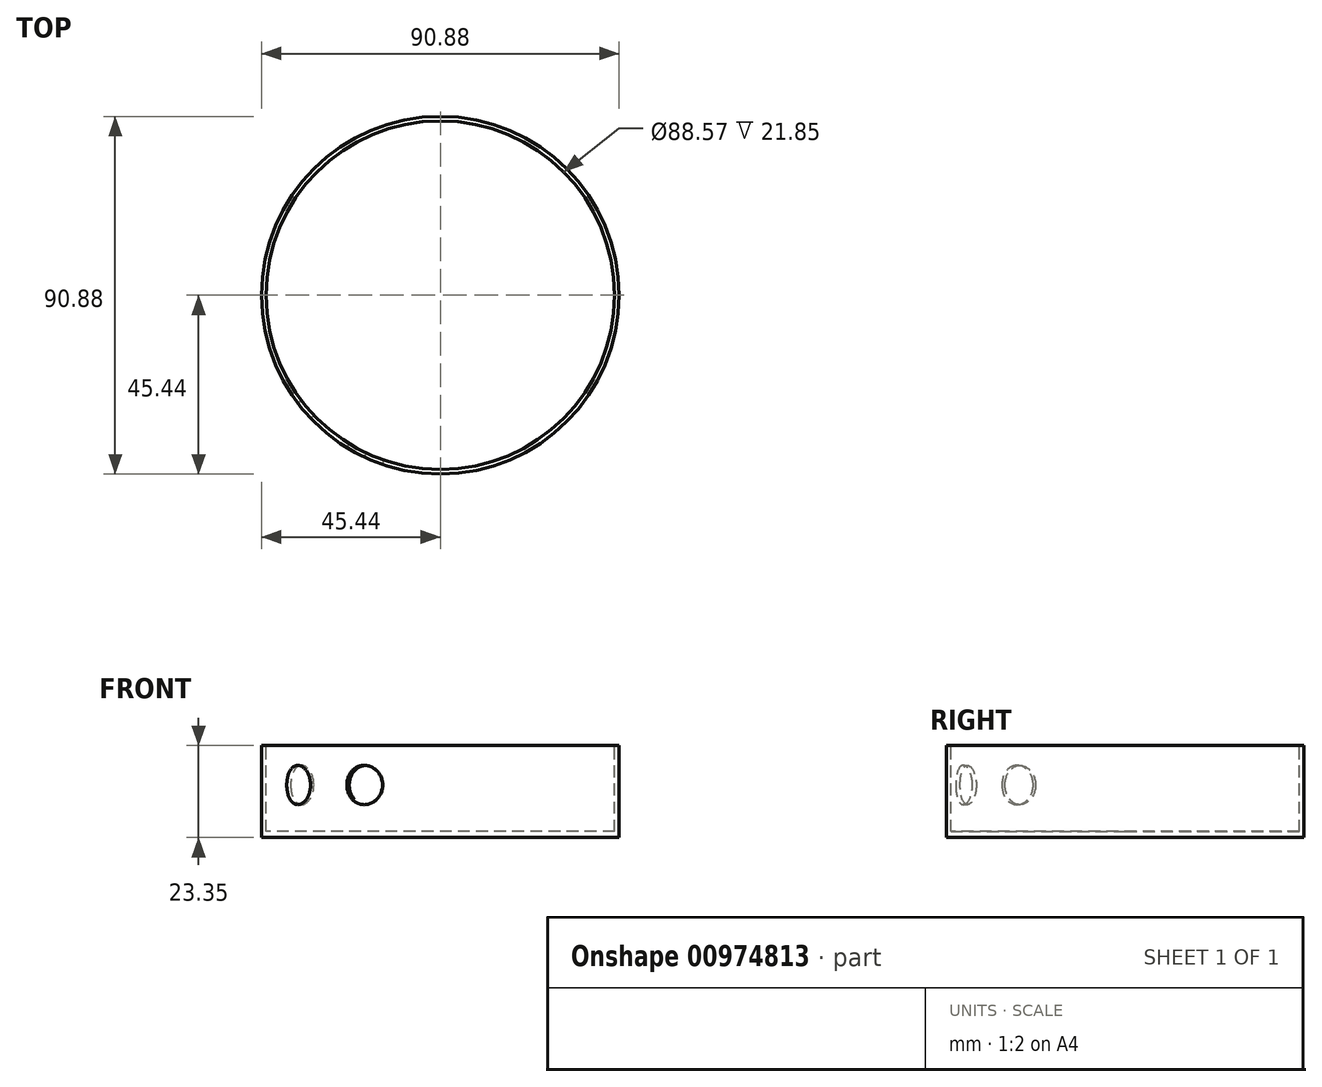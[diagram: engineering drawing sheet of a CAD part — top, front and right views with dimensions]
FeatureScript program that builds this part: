
annotation { "Feature Type Name" : "Feature", "Feature Type Description" : "" }
export const myFeature = defineFeature(function(context is Context, id is Id, definition is map)
    precondition{}
    {
        {
            var Q0;
            Q0=qCreatedBy(makeId("Top.planeOp"),FACE);
            var sketch = newSketch(context, id + "F0", { "sketchPlane" : qUnion([Q0])});
            skCircle(sketch, "E0", {"center": v(0, 0) * mm, "radius": 45.44 * mm});
            skSolve(sketch);
        }
        {
            var Q0;
            Q0 = qSketchRegion(id + "F0", true);
            extrude(context, id + "F1", {"entities" : qUnion([Q0]), "depth" : 23.35 * mm, "offsetDistance" : 25 * mm});
        }
        {
            var Q0;
            Q0=makeQuery(id+"F1.opExtrude","CAP_FACE",FACE,{"disambiguationData":[OSD([sQuery(id+"F0.wireOp",EDGE,"E0")])],"isStart":false});
            var sketch = newSketch(context, id + "F2", { "sketchPlane" : qUnion([Q0])});
            skCircle(sketch, "E1", {"center": v(0, 0) * mm, "radius": 44.29 * mm});
            skSolve(sketch);
        }
        {
            var Q0;
            Q0 = qSketchRegion(id + "F2", true);
            extrude(context, id + "F3", {"entities" : qUnion([Q0]), "operationType" : NewBodyOperationType.REMOVE, "oppositeDirection" : true, "depth" : 23.35 * mm - 1.5 * mm, "offsetDistance" : 25 * mm});
        }
        {
            var Q0;
            Q0=makeQuery(id+"F1.opExtrude","CAP_FACE",FACE,{"disambiguationData":[OSD([sQuery(id+"F0.wireOp",EDGE,"E0")])],"isStart":false});
            var sketch = newSketch(context, id + "F4", { "sketchPlane" : qUnion([Q0])});
            skSolve(sketch);
        }
        {
            var Q0;
            Q0=makeQuery(id+"F4.imprint","IMPRINT",FACE,{"disambiguationData":[TD([[makeQuery(id+"F4.imprint","IMPRINT",EDGE,{"derivedFrom":makeQuery(id+"F1.opExtrude","CAP_EDGE",EDGE,{"disambiguationData":[OSD([sQuery(id+"F0.wireOp",EDGE,"E0")])],"isStart":false})}),1.0]])]});
            var sketch = newSketch(context, id + "F5", { "sketchPlane" : qUnion([Q0])});
            skLineSegment(sketch, "E2", {"start": v(0, 0) * mm, "end": v(-23.74, -38.74) * mm});
            skLineSegment(sketch, "E3", {"start": v(0, 0) * mm, "end": v(-14.69, -43) * mm});
            skArc(sketch, "E4", {"start": v(-23.74, -38.74) * mm, "mid": v(-19.33, -41.12) * mm, "end": v(-14.69, -43) * mm});
            skLineSegment(sketch, "E5.2.0", {"start": v(0, 0) * mm, "end": v(-32.95, -31.28) * mm});
            skLineSegment(sketch, "E5.2.1", {"start": v(0, 0) * mm, "end": v(-39, -23.31) * mm});
            skArc(sketch, "E6", {"start": v(-39, -23.31) * mm, "mid": v(-42.8, -32.48) * mm, "end": v(-32.95, -31.28) * mm});
            skSolve(sketch);
        }
        {
            var Q0;
            Q0 = qSketchRegion(id + "F5", true);
            extrude(context, id + "F6", {"entities" : qUnion([Q0]), "operationType" : NewBodyOperationType.REMOVE, "oppositeDirection" : true, "depth" : 15 * mm, "offsetDistance" : 25 * mm});
        }
        {
            var Q0;
            Q0=makeQuery(id+"F4.imprint","IMPRINT",FACE,{"disambiguationData":[TD([[makeQuery(id+"F4.imprint","IMPRINT",EDGE,{"derivedFrom":makeQuery(id+"F1.opExtrude","CAP_EDGE",EDGE,{"disambiguationData":[OSD([sQuery(id+"F0.wireOp",EDGE,"E0")])],"isStart":false})}),1.0]])]});
            var sketch = newSketch(context, id + "F7", { "sketchPlane" : qUnion([Q0])});
            skCircle(sketch, "E7", {"center": v(0, 0) * mm, "radius": 44.29 * mm});
            skCircle(sketch, "E8", {"center": v(0, 0) * mm, "radius": 45.44 * mm});
            skPoint(sketch, "E9", {"position": v(-14.32, -41.9) * mm});
            skPoint(sketch, "E10", {"position": v(-14.7, -43) * mm});
            skSolve(sketch);
        }
        {
            var Q0;
            {var subQ0=sQuery(id+"F7.wireOp",EDGE,"lr358FzO-w6J5-zg0p-Qxm3-03FLZYF2ygZf");var subQ1=sQuery(id+"F7.wireOp",EDGE,"E7");var subQ2=makeQuery(id+"F7.imprint","INTERSECT",VERTEX,{"derivedFrom":[subQ1,subQ0]});Q0=makeQuery(id+"F7.imprint","IMPRINT",FACE,{"disambiguationData":[TD([[makeQuery(id+"F7.imprint","IMPRINT",EDGE,{"disambiguationData":[TD([[subQ2,-1.0]])],"derivedFrom":subQ1}),-1.0]])]});}
            extrude(context, id + "F8", {"entities" : qUnion([Q0]), "operationType" : NewBodyOperationType.ADD, "oppositeDirection" : true, "depth" : 5 * mm, "offsetDistance" : 25 * mm});
        }
        {
            var Q0;
            Q0=makeQuery(id+"F8.boolean.opBoolean","INTERSECT",EDGE,{"derivedFrom":[makeQuery(id+"F6.boolean.opBoolean","COPY",FACE,{"derivedFrom":makeQuery(id+"F6.opExtrude","SWEPT_FACE",FACE,{"disambiguationData":[OSD([sQuery(id+"F5.wireOp",EDGE,"E5.2.1")])]})}),makeQuery(id+"F8.opExtrude","CAP_FACE",FACE,{"disambiguationData":[OSD([sQuery(id+"F7.wireOp",EDGE,"E7"),sQuery(id+"F7.wireOp",EDGE,"E8")])],"isStart":false})]});
            var Q1;
            Q1=makeQuery(id+"F6.boolean.opBoolean","COPY",EDGE,{"derivedFrom":makeQuery(id+"F6.opExtrude","CAP_EDGE",EDGE,{"disambiguationData":[OSD([sQuery(id+"F5.wireOp",EDGE,"E5.2.1")])],"isStart":false})});
            var Q2;
            Q2=makeQuery(id+"F6.boolean.opBoolean","COPY",EDGE,{"derivedFrom":makeQuery(id+"F6.opExtrude","CAP_EDGE",EDGE,{"disambiguationData":[OSD([sQuery(id+"F5.wireOp",EDGE,"E5.2.0")])],"isStart":false})});
            var Q3;
            Q3=makeQuery(id+"F8.boolean.opBoolean","INTERSECT",EDGE,{"derivedFrom":[makeQuery(id+"F6.boolean.opBoolean","COPY",FACE,{"derivedFrom":makeQuery(id+"F6.opExtrude","SWEPT_FACE",FACE,{"disambiguationData":[OSD([sQuery(id+"F5.wireOp",EDGE,"E5.2.0")])]})}),makeQuery(id+"F8.opExtrude","CAP_FACE",FACE,{"disambiguationData":[OSD([sQuery(id+"F7.wireOp",EDGE,"E7"),sQuery(id+"F7.wireOp",EDGE,"E8")])],"isStart":false})]});
            var Q4;
            Q4=makeQuery(id+"F6.boolean.opBoolean","COPY",EDGE,{"derivedFrom":makeQuery(id+"F6.opExtrude","CAP_EDGE",EDGE,{"disambiguationData":[OSD([sQuery(id+"F5.wireOp",EDGE,"E2")])],"isStart":false})});
            var Q5;
            Q5=makeQuery(id+"F8.boolean.opBoolean","INTERSECT",EDGE,{"derivedFrom":[makeQuery(id+"F6.boolean.opBoolean","COPY",FACE,{"derivedFrom":makeQuery(id+"F6.opExtrude","SWEPT_FACE",FACE,{"disambiguationData":[OSD([sQuery(id+"F5.wireOp",EDGE,"E2")])]})}),makeQuery(id+"F8.opExtrude","CAP_FACE",FACE,{"disambiguationData":[OSD([sQuery(id+"F7.wireOp",EDGE,"E7"),sQuery(id+"F7.wireOp",EDGE,"E8")])],"isStart":false})]});
            var Q6;
            Q6=makeQuery(id+"F8.boolean.opBoolean","INTERSECT",EDGE,{"derivedFrom":[makeQuery(id+"F6.boolean.opBoolean","COPY",FACE,{"derivedFrom":makeQuery(id+"F6.opExtrude","SWEPT_FACE",FACE,{"disambiguationData":[OSD([sQuery(id+"F5.wireOp",EDGE,"E3")])]})}),makeQuery(id+"F8.opExtrude","CAP_FACE",FACE,{"disambiguationData":[OSD([sQuery(id+"F7.wireOp",EDGE,"E7"),sQuery(id+"F7.wireOp",EDGE,"E8")])],"isStart":false})]});
            var Q7;
            Q7=makeQuery(id+"F6.boolean.opBoolean","COPY",EDGE,{"derivedFrom":makeQuery(id+"F6.opExtrude","CAP_EDGE",EDGE,{"disambiguationData":[OSD([sQuery(id+"F5.wireOp",EDGE,"E3")])],"isStart":false})});
            fillet(context, id + "F9", {"entities" : qUnion([Q0, Q1, Q2, Q3, Q4, Q5, Q6, Q7]), "radius" : 5 * mm, "tangentPropagation" : true, "allowEdgeOverflow" : false});
        }
    });
